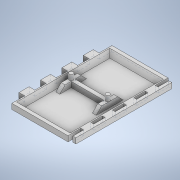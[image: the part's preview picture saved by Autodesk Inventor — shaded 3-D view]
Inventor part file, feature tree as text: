
AUTODESK INVENTOR PART (.ipt)
format: ipt  version: 2020.1 (Build 241239000, 239)  size: 400,896 bytes
history: native  units: mm
features: extrude x8, sketch x8, projected_geometry x5, chamfer x2
ambient origin geometry x8: Origin, YZ Plane, XZ Plane, XY Plane, X Axis, Y Axis, Z Axis, Center Point
bodies: Solid1 (feature_tree)
feature tree (23):
  extrude  "Extrusion1"  Depth=90.0mm
  extrude  "Extrusion2"  Depth=5.419mm
  extrude  "Extrusion3"  Depth=5.419mm
  extrude  "Extrusion4"  Depth=50.0mm
  chamfer  "Chamfer1"  Distance=5.0mm
  extrude  "Tolerances Extrusion "  Depth=3.419mm
  extrude  "Extrusion10"  Depth=2.0mm
  extrude  "Extrusion11"  Depth=4.0mm
  chamfer  "Chamfer3"  Distance=4.0mm
  extrude  "Extrusion12"  Depth=10.0mm
  sketch  "Sketch1"  dims[d0=63.837mm d1=90.0mm]
  sketch  "Sketch2"  dims[d2=5.0mm d3=0.0mm d4=5.419mm]
  sketch  "Sketch3"  dims[d5=10.0mm d6=5.419mm]
  sketch  "Sketch4"  dims[d7=10.0mm d8=50.0mm d10=20.0mm d11=10.0mm d13=10.0mm d15=5.0mm d16=0.0mm]
  projected_geometry  "Projected Loop1"
  sketch  "Sketch9"  dims[d17=90.0mm d18=3.419mm]
  projected_geometry  "Projected Loop10"
  projected_geometry  "Projected Loop11"
  sketch  "Sketch11"  dims[d19=0.0mm d20=2.0mm]
  sketch  "Sketch12"  dims[d21=5.0mm d22=0.0mm d23=5.5mm d24=4.0mm d25=0.0mm]
  projected_geometry  "Projected Loop12"
  sketch  "Sketch13"  dims[d26=4.0mm d27=2.0mm d28=45.0deg d55=0.3mm d56=0.3mm d57=0.3mm d58=0.3mm d59=5.0mm d60=0.0mm d76=3.65mm d77=3.65mm d78=17.05mm d79=17.05mm d80=44.2mm d81=44.2mm d82=10.0mm d83=0.0mm d84=25.0mm d85=25.0mm d86=5.0mm d87=0.0mm d88=5.0mm d89=5.0mm d90=45.0deg d91=2.0mm d92=2.0mm d93=10.0mm d94=0.0mm d61=0.5mm d62=0.872665mm d63=0.5mm d64=0.872665mm]
  projected_geometry  "Projected Loop13"
